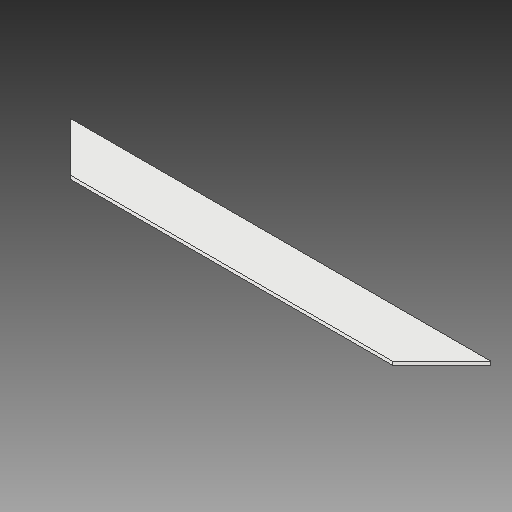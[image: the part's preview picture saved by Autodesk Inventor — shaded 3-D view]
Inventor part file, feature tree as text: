
AUTODESK INVENTOR PART (.ipt)
format: ipt  version: 2018 (Build 220112000, 112)  size: 76,288 bytes
history: native  units: in
note: dims shown in document units (in); Inventor stores cm internally (conversion verified against a paired STEP export)
features: mirror x1
ambient origin geometry x8: Origin, YZ Plane, XZ Plane, XY Plane, X Axis, Y Axis, Z Axis, Center Point
bodies: Solid1 (feature_tree)
feature tree (1):
  mirror  "Mirror1"
